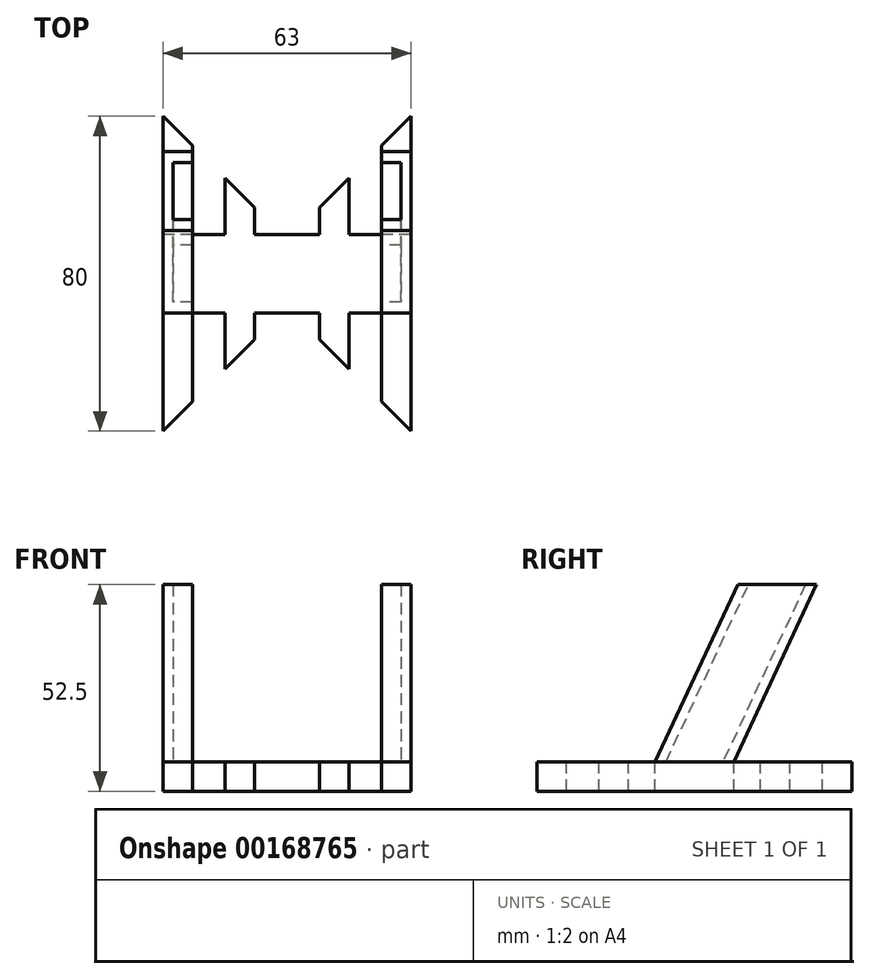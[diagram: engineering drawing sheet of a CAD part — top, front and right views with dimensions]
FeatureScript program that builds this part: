
annotation { "Feature Type Name" : "Feature", "Feature Type Description" : "" }
export const myFeature = defineFeature(function(context is Context, id is Id, definition is map)
    precondition{}
    {
        {
            var Q0;
            Q0=qCreatedBy(makeId("Right.planeOp"),FACE);
            var sketch = newSketch(context, id + "F0", { "sketchPlane" : qUnion([Q0])});
            skLineSegment(sketch, "E0", {"start": v(0, 0) * mm, "end": v(20.98, 45) * mm});
            skLineSegment(sketch, "E1", {"start": v(20.98, 45) * mm, "end": v(40.98, 45) * mm});
            skLineSegment(sketch, "E2", {"start": v(40.98, 45) * mm, "end": v(20, 0) * mm});
            skLineSegment(sketch, "E3", {"start": v(20, 0) * mm, "end": v(0, 0) * mm});
            skLineSegment(sketch, "E4.0", {"start": v(2.76, 0) * mm, "end": v(23.74, 45) * mm});
            skLineSegment(sketch, "E5.0", {"start": v(38.23, 45) * mm, "end": v(17.24, 0) * mm});
            skSolve(sketch);
        }
        {
            var Q0;
            Q0=makeQuery(id+"F0.imprint","IMPRINT",FACE,{"disambiguationData":[TD([[makeQuery(id+"F0.imprint","IMPRINT",EDGE,{"derivedFrom":sQuery(id+"F0.wireOp",EDGE,"E0")}),-1.0]])]});
            var Q1;
            {var subQ0=sQuery(id+"F0.wireOp",EDGE,"E4.0");Q1=makeQuery(id+"F0.imprint","IMPRINT",FACE,{"disambiguationData":[TD([[makeQuery(id+"F0.imprint","IMPRINT",EDGE,{"derivedFrom":subQ0}),-1.0]])]});}
            var Q2;
            {var subQ0=sQuery(id+"F0.wireOp",EDGE,"E2");Q2=makeQuery(id+"F0.imprint","IMPRINT",FACE,{"disambiguationData":[TD([[makeQuery(id+"F0.imprint","IMPRINT",EDGE,{"derivedFrom":subQ0}),-1.0]])]});}
            extrude(context, id + "F1", {"entities" : qUnion([Q0, Q1, Q2]), "endBound" : BoundingType.SYMMETRIC, "depth" : 63 * mm});
        }
        {
            var Q0;
            {var subQ0=sQuery(id+"F0.wireOp",EDGE,"E4.0");Q0=makeQuery(id+"F0.imprint","IMPRINT",FACE,{"disambiguationData":[TD([[makeQuery(id+"F0.imprint","IMPRINT",EDGE,{"derivedFrom":subQ0}),-1.0]])]});}
            extrude(context, id + "F2", {"entities" : qUnion([Q0]), "operationType" : NewBodyOperationType.REMOVE, "endBound" : BoundingType.SYMMETRIC, "depth" : 58 * mm});
        }
        {
            var Q0;
            Q0 = qSketchRegion(id + "F0", true);
            extrude(context, id + "F3", {"entities" : qUnion([Q0]), "operationType" : NewBodyOperationType.REMOVE, "endBound" : BoundingType.SYMMETRIC, "oppositeDirection" : true, "depth" : 48 * mm});
        }
        {
            var Q0;
            Q0=qCreatedBy(makeId("Top.planeOp"),FACE);
            var sketch = newSketch(context, id + "F4", { "sketchPlane" : qUnion([Q0])});
            skLineSegment(sketch, "E6.0", {"start": v(-31.5, 20) * mm, "end": v(-31.5, 0) * mm});
            skLineSegment(sketch, "E7.0", {"start": v(31.5, 20) * mm, "end": v(31.5, 0) * mm});
            skLineSegment(sketch, "E8", {"start": v(-31.5, 0) * mm, "end": v(-31.5, -30) * mm});
            skLineSegment(sketch, "E9.0", {"start": v(-24, 2.76) * mm, "end": v(-24, 0) * mm});
            skLineSegment(sketch, "E10.0", {"start": v(24, 2.76) * mm, "end": v(24, 0) * mm});
            skLineSegment(sketch, "E11", {"start": v(-31.5, -30) * mm, "end": v(-24, -22.5) * mm});
            skLineSegment(sketch, "E12", {"start": v(-24, -22.5) * mm, "end": v(-24, 0) * mm});
            skLineSegment(sketch, "E13.MirrorCS", {"start": v(31.5, -30) * mm, "end": v(24, -22.5) * mm});
            skLineSegment(sketch, "E14.MirrorCS", {"start": v(31.5, 0) * mm, "end": v(31.5, -30) * mm});
            skLineSegment(sketch, "E15.MirrorCS", {"start": v(24, -22.5) * mm, "end": v(24, 0) * mm});
            skLineSegment(sketch, "E16", {"start": v(-31.5, 20) * mm, "end": v(-31.5, 50) * mm});
            skLineSegment(sketch, "E17", {"start": v(-31.5, 50) * mm, "end": v(-24, 42.5) * mm});
            skLineSegment(sketch, "E18", {"start": v(-24, 42.5) * mm, "end": v(-24, 20) * mm});
            skLineSegment(sketch, "E19", {"start": v(-24, 20) * mm, "end": v(24, 20) * mm});
            skLineSegment(sketch, "E20", {"start": v(24, 0) * mm, "end": v(-24, 0) * mm});
            skLineSegment(sketch, "E21.MirrorCS", {"start": v(31.5, 20) * mm, "end": v(31.5, 50) * mm});
            skLineSegment(sketch, "E22.MirrorCS", {"start": v(31.5, 50) * mm, "end": v(24, 42.5) * mm});
            skLineSegment(sketch, "E23.MirrorCS", {"start": v(24, 42.5) * mm, "end": v(24, 20) * mm});
            skLineSegment(sketch, "E24", {"start": v(-15.75, -14.25) * mm, "end": v(-15.75, 0) * mm});
            skLineSegment(sketch, "E25", {"start": v(-8.25, -6.75) * mm, "end": v(-8.25, 0) * mm});
            skLineSegment(sketch, "E26", {"start": v(-15.75, -14.25) * mm, "end": v(-8.25, -6.75) * mm});
            skLineSegment(sketch, "E27.MirrorCS", {"start": v(15.75, -14.25) * mm, "end": v(8.25, -6.75) * mm});
            skLineSegment(sketch, "E28.MirrorCS", {"start": v(15.75, -14.25) * mm, "end": v(15.75, 0) * mm});
            skLineSegment(sketch, "E29.MirrorCS", {"start": v(8.25, -6.75) * mm, "end": v(8.25, 0) * mm});
            skLineSegment(sketch, "E30", {"start": v(-31.5, 10) * mm, "end": v(31.5, 10) * mm, "construction": true});
            skLineSegment(sketch, "E31.MirrorCS", {"start": v(-15.75, 34.25) * mm, "end": v(-8.25, 26.75) * mm});
            skLineSegment(sketch, "E32.MirrorCS", {"start": v(-15.75, 34.25) * mm, "end": v(-15.75, 20) * mm});
            skLineSegment(sketch, "E33.MirrorCS", {"start": v(-8.25, 26.75) * mm, "end": v(-8.25, 20) * mm});
            skLineSegment(sketch, "E34.MirrorCS", {"start": v(15.75, 34.25) * mm, "end": v(8.25, 26.75) * mm});
            skLineSegment(sketch, "E35.MirrorCS", {"start": v(15.75, 34.25) * mm, "end": v(15.75, 20) * mm});
            skLineSegment(sketch, "E36.MirrorCS", {"start": v(8.25, 26.75) * mm, "end": v(8.25, 20) * mm});
            skSolve(sketch);
        }
        {
            var Q0;
            Q0=makeQuery(id+"F4.imprint","IMPRINT",FACE,{"disambiguationData":[TD([[makeQuery(id+"F4.imprint","IMPRINT",EDGE,{"derivedFrom":sQuery(id+"F4.wireOp",EDGE,"E6.0")}),1.0]])]});
            var Q1;
            Q1=makeQuery(id+"F4.imprint","IMPRINT",FACE,{"disambiguationData":[TD([[makeQuery(id+"F4.imprint","IMPRINT",EDGE,{"derivedFrom":sQuery(id+"F4.wireOp",EDGE,"E31.MirrorCS")}),-1.0]])]});
            var Q2;
            {var subQ0=sQuery(id+"F4.wireOp",EDGE,"E24");Q2=makeQuery(id+"F4.imprint","IMPRINT",FACE,{"disambiguationData":[TD([[makeQuery(id+"F4.imprint","IMPRINT",EDGE,{"derivedFrom":subQ0}),-1.0]])]});}
            var Q3;
            Q3=makeQuery(id+"F4.imprint","IMPRINT",FACE,{"disambiguationData":[TD([[makeQuery(id+"F4.imprint","IMPRINT",EDGE,{"derivedFrom":sQuery(id+"F4.wireOp",EDGE,"E27.MirrorCS")}),-1.0]])]});
            var Q4;
            Q4=makeQuery(id+"F4.imprint","IMPRINT",FACE,{"disambiguationData":[TD([[makeQuery(id+"F4.imprint","IMPRINT",EDGE,{"derivedFrom":sQuery(id+"F4.wireOp",EDGE,"E34.MirrorCS")}),1.0]])]});
            extrude(context, id + "F5", {"entities" : qUnion([Q0, Q1, Q2, Q3, Q4]), "oppositeDirection" : true, "depth" : 7.5 * mm});
        }
    });
